# Revit family: DE_MEAKERB_Bridge_basic
name_source: partatom
category: Allgemeines Modell
units: mm (PartAtom-declared; Revit-internal decimal feet)

## family parameters
Beim Laden mit Abzugskörper schneiden = Nein
Bemaßung runder Anschluss = Durchmesser verwenden
Beschriftungsausrichtung beibehalten = Nein
Gemeinsam genutzt = Nein
Kann Basisbauteil für Bewehrung sein = Nein
Raumberechnungspunkt = Nein
Teiletyp = Normal

## types (5) — shared parameters
Ausführungsunterlagen = gemäß Zeichnung und Einzelbeschreibung
Ausschreiben.de = https://ausschreiben.de
Bauelement = Entwässerungsrinnen Oberflächenwasser
Baustoff, Bettung/Fundament = -
Bauteil, Entwässerung = Entwässerungsrinne
Beschreibung = Universal Entwässerungssystem aus Polymerbeton für Belastungsklassen bis D400
Einbautechnologie = siehe Einbauanleitung
Hersteller = MEA Bautechnik GmbH Geschäftsbereich MEA Water Management
Hersteller und Typ - Ausschreibender gleichwertig = wie MEA Bautechnik GmbH, Modell MEA…...
IfcDescription = Universal Entwässerungssystem aus Polymerbeton für Belastungsklassen bis D400
IfcExportAs = IfcWasteTerminalType
IfcExportType = USERDEFINED
Konstruktion Entwässerungsbauteil = Hohlbordrinne für Brücken
MEA Planungshilfe = https://www.mea-group.com
Produktwebsite = https://www.mea-group.com
STLB Bau Mustervorlage = https://www.stlb-bau-online.de
Stutzendurchmesser = 160 mm
Stutzendurchmesser_innen = 156 mm  [stored 0.511811 ft]
Typ Entwässerungsrinne = Typ M
URL = https://www.mea-group.com
guid = cf6c1bd8-9bf4-4563-8c57-07955e2378ac
technische Produktinformation = https://www.mea-group.com
zero-valued in all types: Vorgabe-Ansicht

## per-type parameters (varying)
| type | Deckelexbeginn | Deckelöffnung | Einbauhöhe | Einbauversatz | Halbe Rinnenbreite | Höhe Querschnitt | Kopfstärke | MEA-Artikelnummer | Modell | Nennweite mm Entwässerungsbauteil | Radius Kopf | Rev_Breits | Rev_Position | Revisionsbreite | Revisionslänge | Rinnenbreite | Rinnenhöhe | Sohlstärke | Stutzenanfang | Stutzenlänge | Wandstärke |
| MEAKERB Bridge 160/125 | 130 mm  [stored 0.426509 ft] | 85 mm  [stored 0.278871 ft] | 125 mm  [stored 0.410105 ft] | 75 mm | 110 mm  [stored 0.360892 ft] | 135 mm  [stored 0.442913 ft] | 40 mm  [stored 0.131234 ft] | 010152170 | MEAKERB BRIDGE 160/125 | 160 | 60 mm  [stored 0.19685 ft] | 63 mm | 150 mm | 126 mm | 300 mm | 220 mm | 200 mm | 25 mm  [stored 0.082021 ft] | -75 mm | -225 mm  [stored -0.738189 ft] | 30 mm  [stored 0.0984252 ft] |
| MEAKERB Bridge 160/150 | 155 mm  [stored 0.50853 ft] | 110 mm  [stored 0.360892 ft] | 150 mm | 50 mm  [stored 0.164042 ft] | 110 mm  [stored 0.360892 ft] | 135 mm  [stored 0.442913 ft] | 40 mm  [stored 0.131234 ft] | 010152174 | MEAKERB BRIDGE 160/150 | 160 | 60 mm  [stored 0.19685 ft] | 63 mm | 150 mm | 126 mm | 300 mm | 220 mm | 200 mm | 25 mm  [stored 0.082021 ft] | -50 mm  [stored -0.164042 ft] | -200 mm  [stored -0.656168 ft] | 30 mm  [stored 0.0984252 ft] |
| MEAKERB Bridge 200/75 | 80 mm  [stored 0.262467 ft] | 26 mm | 75 mm | 80 mm  [stored 0.262467 ft] | 140 mm  [stored 0.459318 ft] | 83 mm  [stored 0.27231 ft] | 49 mm | 010152205 | MEAKERB BRIDGE 200/75 | 200 | 10 mm  [stored 0.0328084 ft] | 66 mm  [stored 0.216535 ft] | 142 mm | 132 mm  [stored 0.433071 ft] | 283 mm | 280 mm | 155 mm  [stored 0.50853 ft] | 23 mm  [stored 0.0754593 ft] | -80 mm  [stored -0.262467 ft] | -230 mm  [stored -0.754593 ft] | 40 mm  [stored 0.131234 ft] |
| MEAKERB Bridge 160/125 OPA | 130 mm  [stored 0.426509 ft] | 85 mm  [stored 0.278871 ft] | 125 mm  [stored 0.410105 ft] | 75 mm | 110 mm  [stored 0.360892 ft] | 135 mm  [stored 0.442913 ft] | 40 mm  [stored 0.131234 ft] | 010152184 | MEAKERB BRIDGE 160/125 OPA | 160 | 60 mm  [stored 0.19685 ft] | 63 mm | 150 mm | 126 mm | 300 mm | 220 mm | 200 mm | 25 mm  [stored 0.082021 ft] | -75 mm | -225 mm  [stored -0.738189 ft] | 30 mm  [stored 0.0984252 ft] |
| MEAKERB Bridge 200/75 OPA | 80 mm  [stored 0.262467 ft] | 24 mm | 75 mm | 100 mm  [stored 0.328084 ft] | 140 mm  [stored 0.459318 ft] | 101 mm  [stored 0.331365 ft] | 51 mm | 010152212 | MEAKERB BRIDGE 200/75 OPA | 200 | 20 mm  [stored 0.0656168 ft] | 66 mm  [stored 0.216535 ft] | 142 mm | 132 mm  [stored 0.433071 ft] | 283 mm | 280 mm | 175 mm | 23 mm  [stored 0.0754593 ft] | -100 mm  [stored -0.328084 ft] | -250 mm  [stored -0.82021 ft] | 40 mm  [stored 0.131234 ft] |

note: [stored X ft] marks values corroborated as IEEE doubles in the binary element streams (Revit-internal decimal feet)
